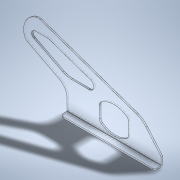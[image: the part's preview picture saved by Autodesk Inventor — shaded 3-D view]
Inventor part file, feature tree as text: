
AUTODESK INVENTOR PART (.ipt)
format: ipt  version: 2020 (Build 240168000, 168)  size: 254,464 bytes
history: native  units: mm
features: other x3, extrude x1
ambient origin geometry x8: Origin, YZ Plane, XZ Plane, XY Plane, X Axis, Y Axis, Z Axis, Center Point
bodies: Body1 (feature_tree)
feature tree (4):
  other  "實體1"
  extrude  "擠出1"  Depth=130.0mm
  other  "折彎零件1"
  other  "定義1"
